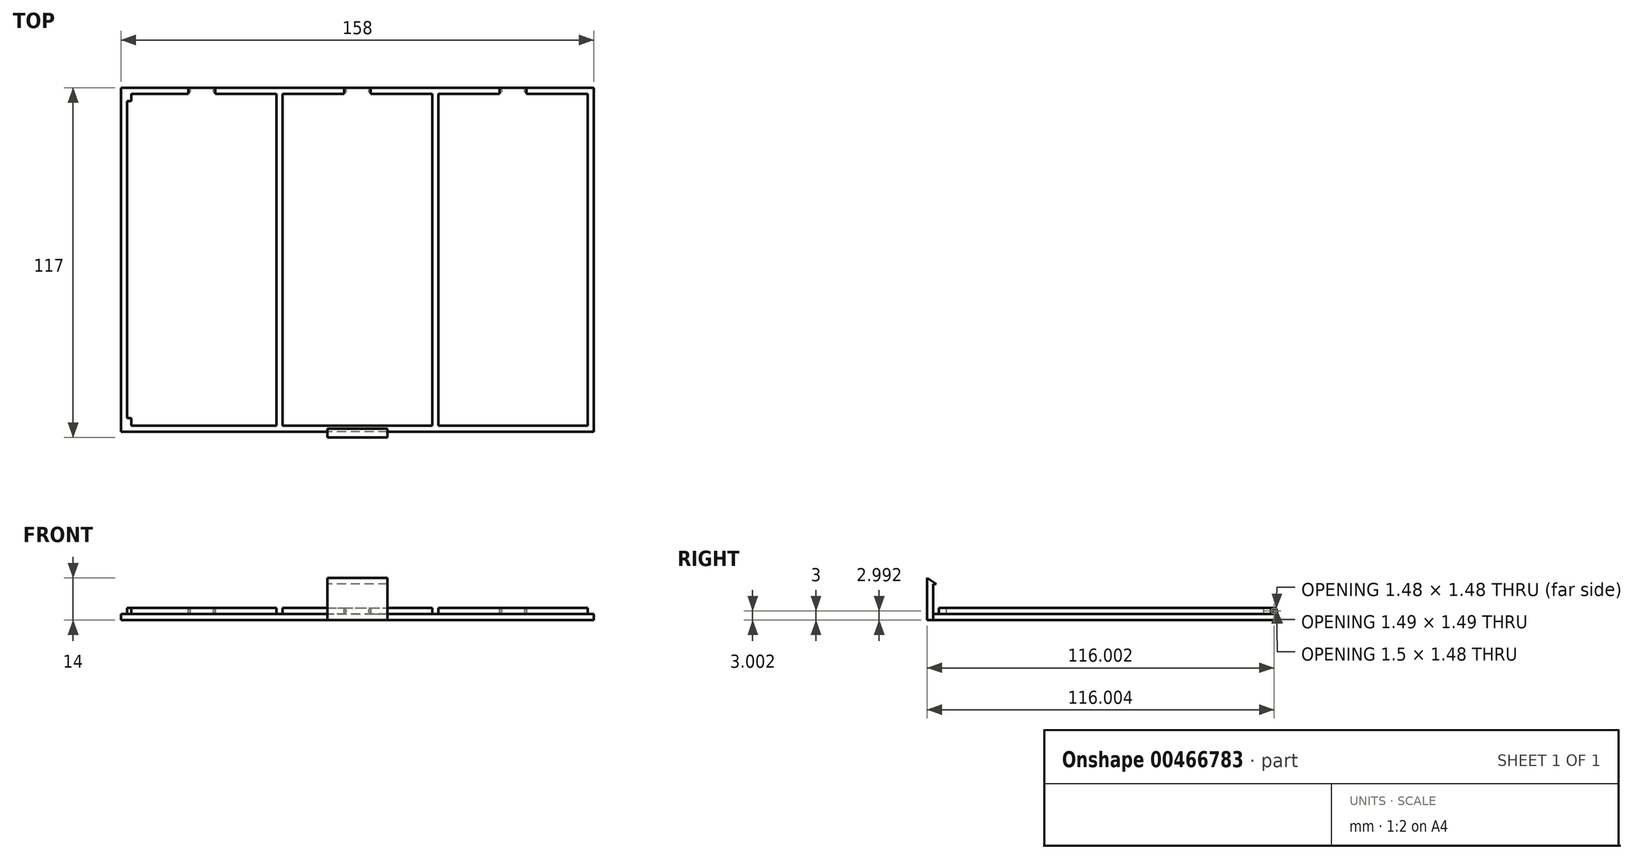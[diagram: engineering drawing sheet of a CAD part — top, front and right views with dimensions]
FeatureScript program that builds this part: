
annotation { "Feature Type Name" : "Feature", "Feature Type Description" : "" }
export const myFeature = defineFeature(function(context is Context, id is Id, definition is map)
    precondition{}
    {
        {
            var Q0;
            Q0=qCreatedBy(makeId("Top.planeOp"),FACE);
            var sketch = newSketch(context, id + "F0", { "sketchPlane" : qUnion([Q0])});
            skLineSegment(sketch, "E0.bottom", {"start": v(-177.63, 18.8) * mm, "end": v(-19.63, 18.8) * mm});
            skLineSegment(sketch, "E0.top", {"start": v(-177.63, -96.2) * mm, "end": v(-19.63, -96.2) * mm});
            skLineSegment(sketch, "E0.left", {"start": v(-177.63, 18.8) * mm, "end": v(-177.63, -96.2) * mm});
            skLineSegment(sketch, "E0.right", {"start": v(-19.63, 18.8) * mm, "end": v(-19.63, -96.2) * mm});
            skSolve(sketch);
        }
        {
            var Q0;
            Q0 = qSketchRegion(id + "F0", true);
            extrude(context, id + "F1", {"entities" : qUnion([Q0]), "depth" : 2 * mm});
        }
        {
            var Q0;
            Q0=makeQuery(id+"F1.opExtrude","CAP_FACE",FACE,{"disambiguationData":[OSD([sQuery(id+"F0.wireOp",EDGE,"E0.bottom"),sQuery(id+"F0.wireOp",EDGE,"E0.top"),sQuery(id+"F0.wireOp",EDGE,"E0.left"),sQuery(id+"F0.wireOp",EDGE,"E0.right")])],"isStart":false});
            var sketch = newSketch(context, id + "F2", { "sketchPlane" : qUnion([Q0])});
            skLineSegment(sketch, "E1.bottom", {"start": v(-175.63, 16.8) * mm, "end": v(-125.63, 16.8) * mm});
            skLineSegment(sketch, "E1.top", {"start": v(-175.63, -94.2) * mm, "end": v(-125.63, -94.2) * mm});
            skLineSegment(sketch, "E1.left", {"start": v(-175.63, 16.8) * mm, "end": v(-175.63, -94.2) * mm});
            skLineSegment(sketch, "E1.right", {"start": v(-125.63, 16.8) * mm, "end": v(-125.63, -94.2) * mm});
            skLineSegment(sketch, "E2.bottom", {"start": v(-123.63, 16.8) * mm, "end": v(-73.63, 16.8) * mm});
            skLineSegment(sketch, "E2.top", {"start": v(-123.63, -94.2) * mm, "end": v(-73.63, -94.2) * mm});
            skLineSegment(sketch, "E2.left", {"start": v(-123.63, 16.8) * mm, "end": v(-123.63, -94.2) * mm});
            skLineSegment(sketch, "E2.right", {"start": v(-73.63, 16.8) * mm, "end": v(-73.63, -94.2) * mm});
            skLineSegment(sketch, "E3.bottom", {"start": v(-71.63, 16.8) * mm, "end": v(-21.63, 16.8) * mm});
            skLineSegment(sketch, "E3.top", {"start": v(-71.63, -94.2) * mm, "end": v(-21.63, -94.2) * mm});
            skLineSegment(sketch, "E3.left", {"start": v(-71.63, 16.8) * mm, "end": v(-71.63, -94.2) * mm});
            skLineSegment(sketch, "E3.right", {"start": v(-21.63, 16.8) * mm, "end": v(-21.63, -94.2) * mm});
            skLineSegment(sketch, "E4.bottom", {"start": v(-155.13, 18.8) * mm, "end": v(-146.13, 18.8) * mm});
            skLineSegment(sketch, "E4.top", {"start": v(-155.13, 16.8) * mm, "end": v(-146.13, 16.8) * mm});
            skLineSegment(sketch, "E4.left", {"start": v(-155.13, 18.8) * mm, "end": v(-155.13, 16.8) * mm});
            skLineSegment(sketch, "E4.right", {"start": v(-146.13, 18.8) * mm, "end": v(-146.13, 16.8) * mm});
            skLineSegment(sketch, "E5.bottom", {"start": v(-51.13, 18.8) * mm, "end": v(-42.13, 18.8) * mm});
            skLineSegment(sketch, "E5.top", {"start": v(-51.13, 16.8) * mm, "end": v(-42.13, 16.8) * mm});
            skLineSegment(sketch, "E5.left", {"start": v(-51.13, 18.8) * mm, "end": v(-51.13, 16.8) * mm});
            skLineSegment(sketch, "E5.right", {"start": v(-42.13, 18.8) * mm, "end": v(-42.13, 16.8) * mm});
            skLineSegment(sketch, "E6.bottom", {"start": v(-103.13, 18.8) * mm, "end": v(-94.13, 18.8) * mm});
            skLineSegment(sketch, "E6.top", {"start": v(-103.13, 16.8) * mm, "end": v(-94.13, 16.8) * mm});
            skLineSegment(sketch, "E6.left", {"start": v(-103.13, 18.8) * mm, "end": v(-103.13, 16.8) * mm});
            skLineSegment(sketch, "E6.right", {"start": v(-94.13, 18.8) * mm, "end": v(-94.13, 16.8) * mm});
            skSolve(sketch);
        }
        {
            var Q0;
            Q0 = qSketchRegion(id + "F2", true);
            extrude(context, id + "F3", {"entities" : qUnion([Q0]), "operationType" : NewBodyOperationType.ADD, "depth" : 2 * mm});
        }
        {
            var Q0;
            Q0=makeQuery(id+"F3.opExtrude","CAP_EDGE",EDGE,{"disambiguationData":[OSD([sQuery(id+"F2.wireOp",EDGE,"E4.bottom")])],"isStart":false});
            var Q1;
            Q1=makeQuery(id+"F3.opExtrude","CAP_EDGE",EDGE,{"disambiguationData":[OSD([sQuery(id+"F2.wireOp",EDGE,"E6.bottom")])],"isStart":false});
            var Q2;
            Q2=makeQuery(id+"F3.opExtrude","CAP_EDGE",EDGE,{"disambiguationData":[OSD([sQuery(id+"F2.wireOp",EDGE,"E5.bottom")])],"isStart":false});
            fillet(context, id + "F4", {"entities" : qUnion([Q0, Q1, Q2]), "radius" : 1 * mm, "tangentPropagation" : true, "allowEdgeOverflow" : false});
        }
        {
            var Q0;
            Q0=makeQuery(id+"F3.opExtrude","SWEPT_FACE",FACE,{"disambiguationData":[OSD([sQuery(id+"F2.wireOp",EDGE,"E4.left")])]});
            var sketch = newSketch(context, id + "F5", { "sketchPlane" : qUnion([Q0])});
            skCircle(sketch, "E7", {"center": v(-17.8, 3) * mm, "radius": 0.75 * mm});
            skLineSegment(sketch, "E8", {"start": v(-18.24, 2.4) * mm, "end": v(-17.37, 3.61) * mm});
            skSolve(sketch);
        }
        {
            var Q0;
            {var subQ0=sQuery(id+"F5.wireOp",EDGE,"E8");Q0=makeQuery(id+"F5.imprint","IMPRINT",FACE,{"disambiguationData":[TD([[makeQuery(id+"F5.imprint","IMPRINT",EDGE,{"derivedFrom":subQ0}),1.0]])]});}
            var Q1;
            Q1=sQuery(id+"F5.wireOp",EDGE,"E8");
            revolve(context, id + "F6", {"operationType" : NewBodyOperationType.REMOVE, "entities" : qUnion([Q0]), "axis" : qUnion([Q1]), "revolveType" : RevolveType.FULL, "oppositeDirection" : true});
        }
        {
            var Q0;
            Q0=makeQuery(id+"F3.opExtrude","SWEPT_FACE",FACE,{"disambiguationData":[OSD([sQuery(id+"F2.wireOp",EDGE,"E4.right")])]});
            var sketch = newSketch(context, id + "F7", { "sketchPlane" : qUnion([Q0])});
            skCircle(sketch, "E9", {"center": v(17.8, 3) * mm, "radius": 0.75 * mm});
            skLineSegment(sketch, "E10", {"start": v(18.5, 2.72) * mm, "end": v(17.1, 3.26) * mm});
            skSolve(sketch);
        }
        {
            var Q0;
            {var subQ0=sQuery(id+"F7.wireOp",EDGE,"E10");Q0=makeQuery(id+"F7.imprint","IMPRINT",FACE,{"disambiguationData":[TD([[makeQuery(id+"F7.imprint","IMPRINT",EDGE,{"derivedFrom":subQ0}),-1.0]])]});}
            var Q1;
            Q1=sQuery(id+"F7.wireOp",EDGE,"E10");
            revolve(context, id + "F8", {"operationType" : NewBodyOperationType.REMOVE, "entities" : qUnion([Q0]), "axis" : qUnion([Q1]), "revolveType" : RevolveType.FULL, "oppositeDirection" : true});
        }
        {
            var Q0;
            Q0=makeQuery(id+"F3.opExtrude","SWEPT_FACE",FACE,{"disambiguationData":[OSD([sQuery(id+"F2.wireOp",EDGE,"E6.left")])]});
            var sketch = newSketch(context, id + "F9", { "sketchPlane" : qUnion([Q0])});
            skCircle(sketch, "E11", {"center": v(-17.8, 3) * mm, "radius": 0.75 * mm});
            skLineSegment(sketch, "E12", {"start": v(-18.22, 2.38) * mm, "end": v(-17.38, 3.62) * mm});
            skSolve(sketch);
        }
        {
            var Q0;
            {var subQ0=sQuery(id+"F9.wireOp",EDGE,"E12");Q0=makeQuery(id+"F9.imprint","IMPRINT",FACE,{"disambiguationData":[TD([[makeQuery(id+"F9.imprint","IMPRINT",EDGE,{"derivedFrom":subQ0}),1.0]])]});}
            var Q1;
            Q1=sQuery(id+"F9.wireOp",EDGE,"E12");
            revolve(context, id + "F10", {"operationType" : NewBodyOperationType.REMOVE, "entities" : qUnion([Q0]), "axis" : qUnion([Q1]), "revolveType" : RevolveType.FULL, "oppositeDirection" : true});
        }
        {
            var Q0;
            Q0=makeQuery(id+"F3.opExtrude","SWEPT_FACE",FACE,{"disambiguationData":[OSD([sQuery(id+"F2.wireOp",EDGE,"E6.right")])]});
            var sketch = newSketch(context, id + "F11", { "sketchPlane" : qUnion([Q0])});
            skCircle(sketch, "E13", {"center": v(17.8, 3) * mm, "radius": 0.75 * mm});
            skLineSegment(sketch, "E14", {"start": v(18.17, 2.35) * mm, "end": v(17.43, 3.65) * mm});
            skSolve(sketch);
        }
        {
            var Q0;
            {var subQ0=sQuery(id+"F11.wireOp",EDGE,"E14");Q0=makeQuery(id+"F11.imprint","IMPRINT",FACE,{"disambiguationData":[TD([[makeQuery(id+"F11.imprint","IMPRINT",EDGE,{"derivedFrom":subQ0}),-1.0]])]});}
            var Q1;
            Q1=sQuery(id+"F11.wireOp",EDGE,"E14");
            revolve(context, id + "F12", {"operationType" : NewBodyOperationType.REMOVE, "entities" : qUnion([Q0]), "axis" : qUnion([Q1]), "revolveType" : RevolveType.FULL, "oppositeDirection" : true});
        }
        {
            var Q0;
            Q0=makeQuery(id+"F3.opExtrude","SWEPT_FACE",FACE,{"disambiguationData":[OSD([sQuery(id+"F2.wireOp",EDGE,"E5.left")])]});
            var sketch = newSketch(context, id + "F13", { "sketchPlane" : qUnion([Q0])});
            skCircle(sketch, "E15", {"center": v(-17.8, 3) * mm, "radius": 0.75 * mm});
            skLineSegment(sketch, "E16", {"start": v(-18.47, 2.66) * mm, "end": v(-17.13, 3.34) * mm});
            skSolve(sketch);
        }
        {
            var Q0;
            {var subQ0=sQuery(id+"F13.wireOp",EDGE,"E16");Q0=makeQuery(id+"F13.imprint","IMPRINT",FACE,{"disambiguationData":[TD([[makeQuery(id+"F13.imprint","IMPRINT",EDGE,{"derivedFrom":subQ0}),1.0]])]});}
            var Q1;
            Q1=sQuery(id+"F13.wireOp",EDGE,"E16");
            revolve(context, id + "F14", {"operationType" : NewBodyOperationType.REMOVE, "entities" : qUnion([Q0]), "axis" : qUnion([Q1]), "revolveType" : RevolveType.FULL, "oppositeDirection" : true});
        }
        {
            var Q0;
            Q0=makeQuery(id+"F3.opExtrude","SWEPT_FACE",FACE,{"disambiguationData":[OSD([sQuery(id+"F2.wireOp",EDGE,"E5.right")])]});
            var sketch = newSketch(context, id + "F15", { "sketchPlane" : qUnion([Q0])});
            skCircle(sketch, "E17", {"center": v(17.8, 3) * mm, "radius": 0.75 * mm});
            skLineSegment(sketch, "E18", {"start": v(18.55, 3) * mm, "end": v(17.05, 3) * mm});
            skSolve(sketch);
        }
        {
            var Q0;
            {var subQ0=sQuery(id+"F15.wireOp",EDGE,"E18");Q0=makeQuery(id+"F15.imprint","IMPRINT",FACE,{"disambiguationData":[TD([[makeQuery(id+"F15.imprint","IMPRINT",EDGE,{"derivedFrom":subQ0}),1.0]])]});}
            var Q1;
            Q1=sQuery(id+"F15.wireOp",EDGE,"E18");
            revolve(context, id + "F16", {"operationType" : NewBodyOperationType.REMOVE, "entities" : qUnion([Q0]), "axis" : qUnion([Q1]), "revolveType" : RevolveType.FULL, "oppositeDirection" : true});
        }
        {
            var Q0;
            Q0=makeQuery(id+"F3.opExtrude","CAP_FACE",FACE,{"disambiguationData":[OSD([sQuery(id+"F2.wireOp",EDGE,"E1.bottom"),sQuery(id+"F2.wireOp",EDGE,"E1.top"),sQuery(id+"F2.wireOp",EDGE,"E1.left"),sQuery(id+"F2.wireOp",EDGE,"E1.right"),sQuery(id+"F2.wireOp",EDGE,"E4.bottom"),sQuery(id+"F2.wireOp",EDGE,"E4.left"),sQuery(id+"F2.wireOp",EDGE,"E4.right")])],"isStart":false});
            var sketch = newSketch(context, id + "F17", { "sketchPlane" : qUnion([Q0])});
            skLineSegment(sketch, "E19.bottom", {"start": v(-175.63, 16.8) * mm, "end": v(-174.13, 16.8) * mm});
            skLineSegment(sketch, "E19.top", {"start": v(-175.63, 14.3) * mm, "end": v(-174.13, 14.3) * mm});
            skLineSegment(sketch, "E19.left", {"start": v(-175.63, 16.8) * mm, "end": v(-175.63, 14.3) * mm});
            skLineSegment(sketch, "E19.right", {"start": v(-174.13, 16.8) * mm, "end": v(-174.13, 14.3) * mm});
            skLineSegment(sketch, "E20.bottom", {"start": v(-175.63, -94.2) * mm, "end": v(-174.13, -94.2) * mm});
            skLineSegment(sketch, "E20.top", {"start": v(-175.63, -91.7) * mm, "end": v(-174.13, -91.7) * mm});
            skLineSegment(sketch, "E20.left", {"start": v(-175.63, -94.2) * mm, "end": v(-175.63, -91.7) * mm});
            skLineSegment(sketch, "E20.right", {"start": v(-174.13, -94.2) * mm, "end": v(-174.13, -91.7) * mm});
            skSolve(sketch);
        }
        {
            var Q0;
            Q0 = qSketchRegion(id + "F17", true);
            extrude(context, id + "F18", {"entities" : qUnion([Q0]), "operationType" : NewBodyOperationType.REMOVE, "oppositeDirection" : true, "depth" : 2 * mm});
        }
        {
            var Q0;
            Q0=makeQuery(id+"F1.opExtrude","SWEPT_FACE",FACE,{"disambiguationData":[OSD([sQuery(id+"F0.wireOp",EDGE,"E0.top")])]});
            var sketch = newSketch(context, id + "F19", { "sketchPlane" : qUnion([Q0])});
            skLineSegment(sketch, "E21.bottom", {"start": v(-108.63, 0) * mm, "end": v(-88.63, 0) * mm});
            skLineSegment(sketch, "E21.top", {"start": v(-108.63, 14) * mm, "end": v(-88.63, 14) * mm});
            skLineSegment(sketch, "E21.left", {"start": v(-108.63, 0) * mm, "end": v(-108.63, 14) * mm});
            skLineSegment(sketch, "E21.right", {"start": v(-88.63, 0) * mm, "end": v(-88.63, 14) * mm});
            skSolve(sketch);
        }
        {
            var Q0;
            Q0 = qSketchRegion(id + "F19", true);
            extrude(context, id + "F20", {"entities" : qUnion([Q0]), "operationType" : NewBodyOperationType.ADD, "endBound" : BoundingType.SYMMETRIC, "depth" : 4 * mm});
        }
        {
            var Q0;
            Q0=makeQuery(id+"F20.opExtrude","SWEPT_FACE",FACE,{"disambiguationData":[OSD([sQuery(id+"F19.wireOp",EDGE,"E21.left")])]});
            var sketch = newSketch(context, id + "F21", { "sketchPlane" : qUnion([Q0])});
            skLineSegment(sketch, "E22.bottom", {"start": v(94.2, 2) * mm, "end": v(96.2, 2) * mm});
            skLineSegment(sketch, "E22.top", {"start": v(94.2, 12) * mm, "end": v(96.2, 12) * mm});
            skLineSegment(sketch, "E22.left", {"start": v(94.2, 2) * mm, "end": v(94.2, 12) * mm});
            skLineSegment(sketch, "E22.right", {"start": v(96.2, 2) * mm, "end": v(96.2, 12) * mm});
            skLineSegment(sketch, "E23", {"start": v(98.2, 14) * mm, "end": v(94.2, 14) * mm});
            skLineSegment(sketch, "E24", {"start": v(94.2, 14) * mm, "end": v(94.2, 12) * mm});
            skLineSegment(sketch, "E25", {"start": v(94.2, 12) * mm, "end": v(95.2, 12) * mm});
            skLineSegment(sketch, "E26", {"start": v(95.2, 12) * mm, "end": v(98.2, 14) * mm});
            skSolve(sketch);
        }
        {
            var Q0;
            Q0 = qSketchRegion(id + "F21", true);
            extrude(context, id + "F22", {"entities" : qUnion([Q0]), "operationType" : NewBodyOperationType.REMOVE, "oppositeDirection" : true, "depth" : 25 * mm});
        }
    });
